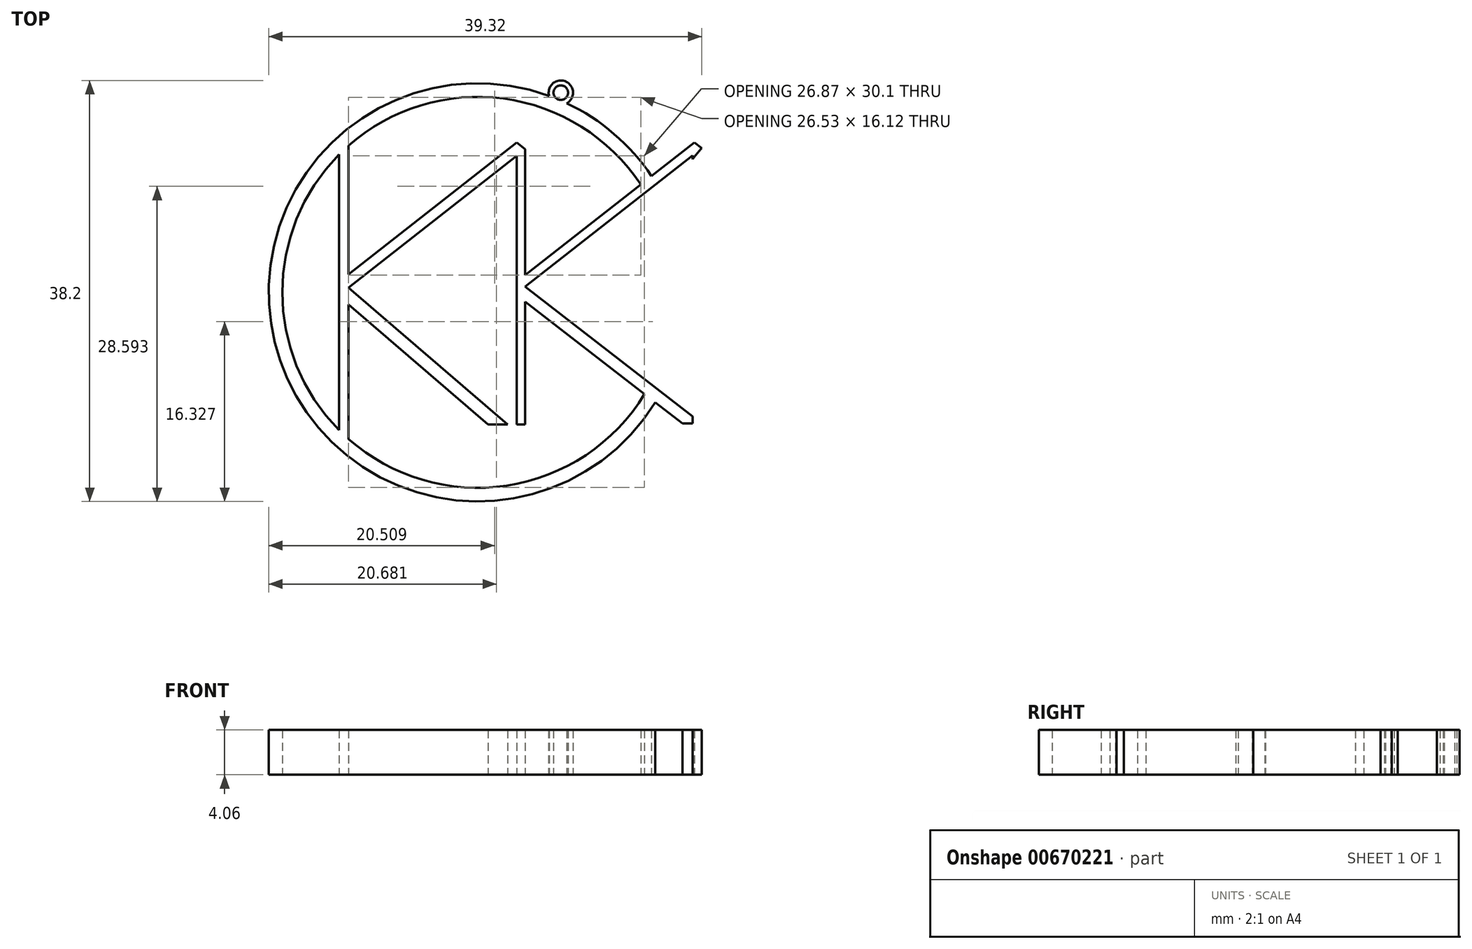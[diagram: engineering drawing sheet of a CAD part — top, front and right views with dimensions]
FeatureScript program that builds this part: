
annotation { "Feature Type Name" : "Feature", "Feature Type Description" : "" }
export const myFeature = defineFeature(function(context is Context, id is Id, definition is map)
    precondition{}
    {
        {
            var Q0;
            Q0=qCreatedBy(makeId("Top.planeOp"),FACE);
            var sketch = newSketch(context, id + "F0", { "sketchPlane" : qUnion([Q0])});
            skLineSegment(sketch, "E0", {"start": v(-55.4, 46.99) * mm, "end": v(-55.4, 35.7) * mm});
            skLineSegment(sketch, "E1.1.0.0", {"start": v(-39.37, 47.07) * mm, "end": v(-39.37, 35.63) * mm});
            skLineSegment(sketch, "E1.2.0.0", {"start": v(-23.33, 33.38) * mm, "end": v(-23.33, 22.18) * mm});
            skLineSegment(sketch, "E1.direction1", {"start": v(-55.4, 22.01) * mm, "end": v(-39.37, 22.1) * mm, "construction": true});
            skLineSegment(sketch, "E2", {"start": v(-55.4, 34.5) * mm, "end": v(-40.97, 22.09) * mm});
            skLineSegment(sketch, "E3", {"start": v(-39.37, 34.59) * mm, "end": v(-24.17, 22.83) * mm});
            skLineSegment(sketch, "E4", {"start": v(-55.4, 34.5) * mm, "end": v(-40.13, 46.48) * mm});
            skLineSegment(sketch, "E5", {"start": v(-39.37, 34.59) * mm, "end": v(-24.17, 46.5) * mm});
            skLineSegment(sketch, "E6", {"start": v(-23.33, 34.59) * mm, "end": v(-8.91, 22.18) * mm});
            skLineSegment(sketch, "E7", {"start": v(-23.33, 46.44) * mm, "end": v(-23.33, 35.48) * mm});
            skFitSpline(sketch, "E8", {"points": [v(-15.28, 40.35) * mm, v(-15.27, 40.36) * mm], "startDerivative": vector(0, 0) * mm, "endDerivative": vector(0, 0) * mm});
            skFitSpline(sketch, "E9", {"points": [v(-23.33, 47.16) * mm, v(-10.38, 47.16) * mm, v(-13.12, 36.69) * mm, v(-23.33, 34.59) * mm, v(-23.33, 47.16) * mm]});
            skArc(sketch, "E10", {"start": v(-28.88, 43.86) * mm, "mid": v(-61.41, 33.75) * mm, "end": v(-28.53, 24.84) * mm});
            skArc(sketch, "E11", {"start": v(-27.9, 44.62) * mm, "mid": v(-31.3, 48.45) * mm, "end": v(-35.59, 51.24) * mm});
            skLineSegment(sketch, "E12", {"start": v(-56.25, 46.59) * mm, "end": v(-56.25, 22.01) * mm});
            skLineSegment(sketch, "E13", {"start": v(-55.4, 35.7) * mm, "end": v(-40.13, 47.68) * mm});
            skLineSegment(sketch, "E14", {"start": v(-40.13, 47.68) * mm, "end": v(-39.37, 47.07) * mm});
            skLineSegment(sketch, "E15", {"start": v(-55.4, 32.99) * mm, "end": v(-42.72, 22.08) * mm});
            skLineSegment(sketch, "E16", {"start": v(-42.72, 22.08) * mm, "end": v(-40.97, 22.09) * mm});
            skLineSegment(sketch, "E17", {"start": v(-40.13, 46.48) * mm, "end": v(-40.13, 22.09) * mm});
            skLineSegment(sketch, "E18", {"start": v(-39.37, 35.63) * mm, "end": v(-24, 47.68) * mm});
            skLineSegment(sketch, "E19", {"start": v(-24, 47.68) * mm, "end": v(-23.33, 47.16) * mm});
            skLineSegment(sketch, "E20", {"start": v(-39.37, 33.22) * mm, "end": v(-28.53, 24.84) * mm});
            skLineSegment(sketch, "E21", {"start": v(-25.1, 22.18) * mm, "end": v(-23.33, 22.18) * mm});
            skLineSegment(sketch, "E22", {"start": v(-24.17, 46.5) * mm, "end": v(-24.17, 22.18) * mm});
            skLineSegment(sketch, "E23", {"start": v(-24.17, 22.18) * mm, "end": v(-23.33, 22.18) * mm});
            skLineSegment(sketch, "E24", {"start": v(-23.33, 33.38) * mm, "end": v(-10.32, 22.18) * mm});
            skLineSegment(sketch, "E25", {"start": v(-10.32, 22.18) * mm, "end": v(-8.91, 22.18) * mm});
            skFitSpline(sketch, "E26", {"points": [v(-23.33, 46.44) * mm, v(-11.08, 46.9) * mm, v(-13.96, 37.58) * mm, v(-23.33, 35.48) * mm, v(-23.33, 46.44) * mm]});
            skLineSegment(sketch, "E27.trimOffspring", {"start": v(-27.55, 24.08) * mm, "end": v(-25.1, 22.18) * mm});
            skLineSegment(sketch, "E28.trimOffspring", {"start": v(-39.37, 33.22) * mm, "end": v(-39.37, 22.1) * mm});
            skLineSegment(sketch, "E29.trimOffspring", {"start": v(-55.4, 32.99) * mm, "end": v(-55.4, 22.01) * mm});
            skLineSegment(sketch, "E30", {"start": v(-55.4, 22.01) * mm, "end": v(-55.4, 20.76) * mm});
            skLineSegment(sketch, "E31", {"start": v(-40.97, 22.09) * mm, "end": v(-39.37, 22.1) * mm});
            skLineSegment(sketch, "E32", {"start": v(-56.25, 22.01) * mm, "end": v(-56.25, 21.57) * mm});
            skCircle(sketch, "E33", {"center": v(-36.13, 52.2) * mm, "radius": 0.66 * mm});
            skArc(sketch, "E34", {"start": v(-35.59, 51.24) * mm, "mid": v(-35.7, 53.22) * mm, "end": v(-37.2, 51.9) * mm});
            skArc(sketch, "E35.trimOffspring", {"start": v(-37.2, 51.9) * mm, "mid": v(-61.6, 27.86) * mm, "end": v(-27.55, 24.08) * mm});
            skLineSegment(sketch, "E36", {"start": v(-55.4, 46.99) * mm, "end": v(-55.4, 47.38) * mm});
            skLineSegment(sketch, "E37", {"start": v(-40.13, 22.09) * mm, "end": v(-40.13, 21.16) * mm});
            skLineSegment(sketch, "E38", {"start": v(-40.13, 21.16) * mm, "end": v(-40.97, 22.09) * mm});
            skLineSegment(sketch, "E39", {"start": v(-39.37, 22.1) * mm, "end": v(-39.36, 20.96) * mm});
            skLineSegment(sketch, "E40", {"start": v(-42.72, 22.08) * mm, "end": v(-41.58, 21.1) * mm});
            skLineSegment(sketch, "E41", {"start": v(-41.58, 21.1) * mm, "end": v(-39.36, 20.96) * mm});
            skLineSegment(sketch, "E42", {"start": v(-40.97, 22.09) * mm, "end": v(-40.13, 21.16) * mm});
            skLineSegment(sketch, "E43", {"start": v(-40.13, 21.16) * mm, "end": v(-40.13, 22.09) * mm});
            skSolve(sketch);
        }
        {
            var Q0;
            Q0=makeQuery(id+"F0.imprint","IMPRINT",FACE,{"disambiguationData":[TD([[makeQuery(id+"F0.imprint","IMPRINT",EDGE,{"derivedFrom":sQuery(id+"F0.wireOp",EDGE,"E0")}),-1.0]])]});
            extrude(context, id + "F1", {"entities" : qUnion([Q0]), "depth" : 4.06 * mm, "offsetDistance" : 25.4 * mm});
        }
    });
